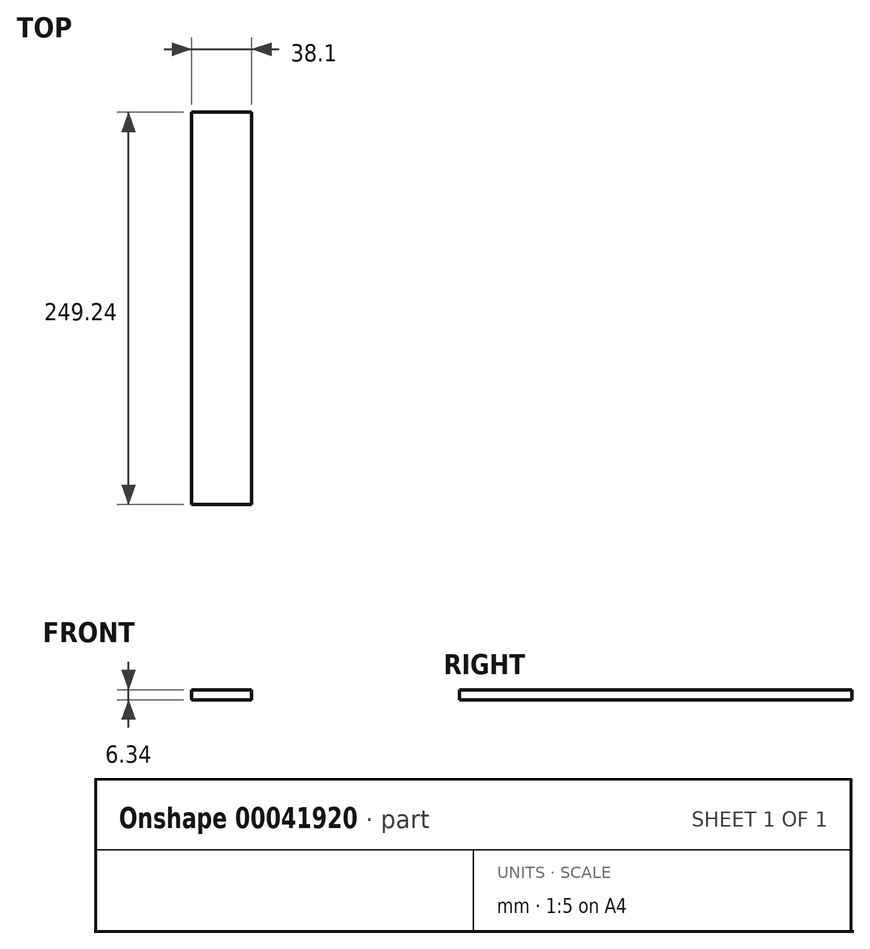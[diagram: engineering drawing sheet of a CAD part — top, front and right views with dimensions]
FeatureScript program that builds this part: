
annotation { "Feature Type Name" : "Feature", "Feature Type Description" : "" }
export const myFeature = defineFeature(function(context is Context, id is Id, definition is map)
    precondition{}
    {
        {
            var Q0;
            Q0=qCreatedBy(makeId("Front.planeOp"),FACE);
            var sketch = newSketch(context, id + "F0", { "sketchPlane" : qUnion([Q0])});
            skLineSegment(sketch, "E0.rect.bottom", {"start": v(19.05, 3.18) * mm, "end": v(-19.05, 3.18) * mm});
            skLineSegment(sketch, "E0.rect.top", {"start": v(19.05, -3.18) * mm, "end": v(-19.05, -3.18) * mm});
            skLineSegment(sketch, "E0.rect.left", {"start": v(19.05, 3.18) * mm, "end": v(19.05, -3.18) * mm});
            skLineSegment(sketch, "E0.rect.right", {"start": v(-19.05, 3.18) * mm, "end": v(-19.05, -3.18) * mm});
            skPoint(sketch, "E0.rect.middle", {"position": v(0, 0) * mm});
            skSolve(sketch);
        }
        {
            var Q0;
            Q0=makeQuery(id+"F0.imprint","IMPRINT",FACE,{"disambiguationData":[TD([[makeQuery(id+"F0.imprint","IMPRINT",EDGE,{"derivedFrom":sQuery(id+"F0.wireOp",EDGE,"E0.rect.bottom")}),1.0]])]});
            extrude(context, id + "F1", {"entities" : qUnion([Q0]), "endBound" : BoundingType.SYMMETRIC, "depth" : 249.24 * mm});
        }
    });
